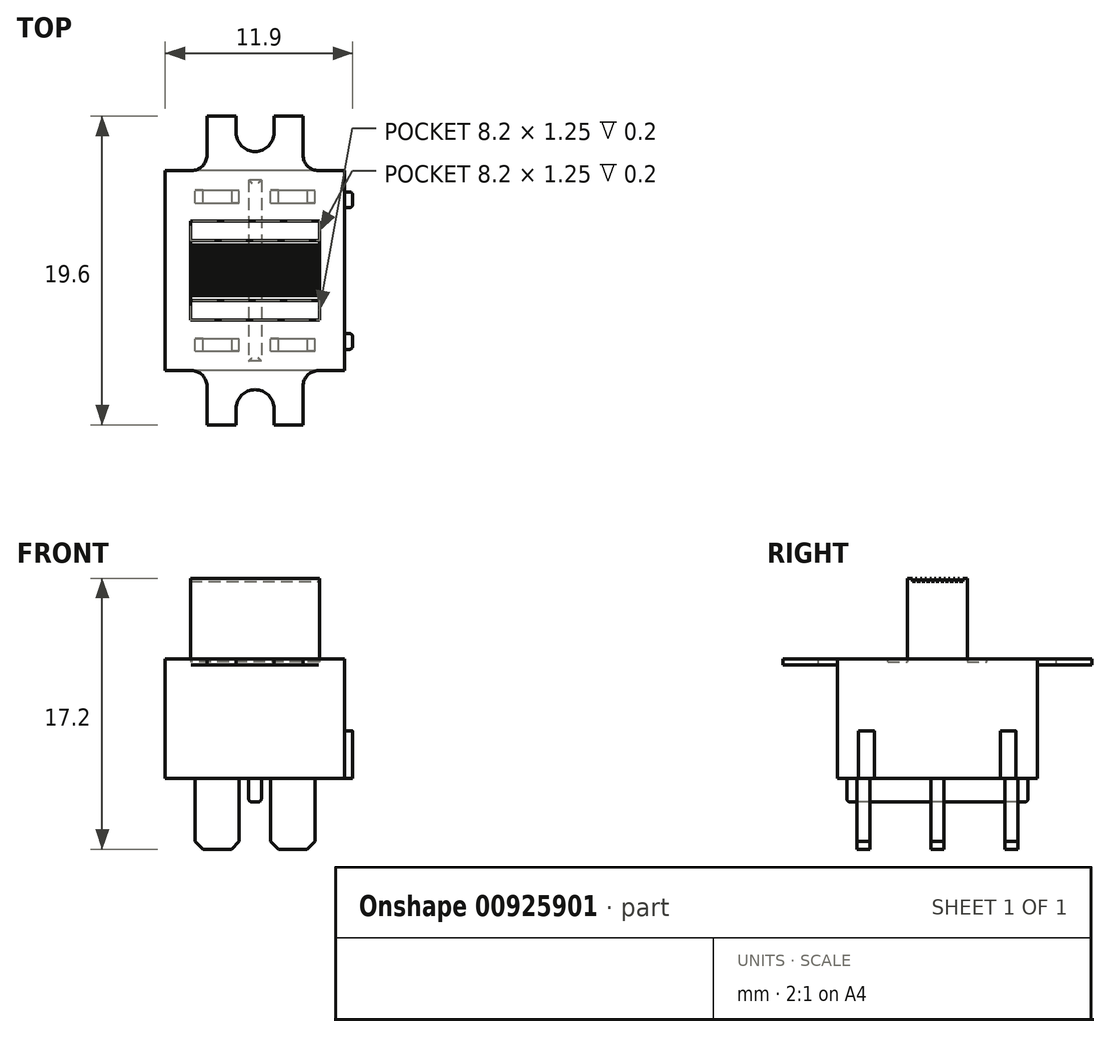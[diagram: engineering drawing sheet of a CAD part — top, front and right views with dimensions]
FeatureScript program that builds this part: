
annotation { "Feature Type Name" : "Feature", "Feature Type Description" : "" }
export const myFeature = defineFeature(function(context is Context, id is Id, definition is map)
    precondition{}
    {
        {
            var Q0;
            Q0=qCreatedBy(makeId("Top.planeOp"),FACE);
            var sketch = newSketch(context, id + "F0", { "sketchPlane" : qUnion([Q0])});
            skLineSegment(sketch, "E0.bottom", {"start": v(5.7, -6.35) * mm, "end": v(-5.7, -6.35) * mm});
            skLineSegment(sketch, "E0.top", {"start": v(5.7, 6.35) * mm, "end": v(-5.7, 6.35) * mm});
            skLineSegment(sketch, "E0.left", {"start": v(5.7, -6.35) * mm, "end": v(5.7, 6.35) * mm});
            skLineSegment(sketch, "E0.right", {"start": v(-5.7, -6.35) * mm, "end": v(-5.7, 6.35) * mm});
            skPoint(sketch, "E0.middle", {"position": v(0, 0) * mm});
            skLineSegment(sketch, "E1.bottom", {"start": v(3.05, -9.8) * mm, "end": v(-3.05, -9.8) * mm});
            skLineSegment(sketch, "E1.top", {"start": v(3.05, 9.8) * mm, "end": v(-3.05, 9.8) * mm});
            skLineSegment(sketch, "E1.left", {"start": v(3.05, -9.8) * mm, "end": v(3.05, 9.8) * mm});
            skLineSegment(sketch, "E1.right", {"start": v(-3.05, -9.8) * mm, "end": v(-3.05, 9.8) * mm});
            skSolve(sketch);
        }
        {
            var Q0;
            Q0 = qSketchRegion(id + "F0", true);
            extrude(context, id + "F1", {"entities" : qUnion([Q0]), "depth" : 0.4 * mm, "offsetDistance" : 25 * mm});
        }
        {
            var Q0;
            Q0=makeQuery(id+"F1.opExtrude","CAP_FACE",FACE,{"disambiguationData":[OSD([sQuery(id+"F0.wireOp",EDGE,"E0.bottom"),sQuery(id+"F0.wireOp",EDGE,"E0.top"),sQuery(id+"F0.wireOp",EDGE,"E0.left"),sQuery(id+"F0.wireOp",EDGE,"E0.right"),sQuery(id+"F0.wireOp",EDGE,"E1.bottom"),sQuery(id+"F0.wireOp",EDGE,"E1.top"),sQuery(id+"F0.wireOp",EDGE,"E1.left"),sQuery(id+"F0.wireOp",EDGE,"E1.right")])],"isStart":false});
            var sketch = newSketch(context, id + "F2", { "sketchPlane" : qUnion([Q0])});
            skLineSegment(sketch, "E2", {"start": v(-4.12, 8.77) * mm, "end": v(4.46, 8.77) * mm, "construction": true});
            skLineSegment(sketch, "E3", {"start": v(-3.99, -8.77) * mm, "end": v(4.43, -8.77) * mm, "construction": true});
            skArc(sketch, "E4", {"start": v(1.2, 8.77) * mm, "mid": v(0, 7.57) * mm, "end": v(-1.2, 8.77) * mm});
            skArc(sketch, "E5", {"start": v(1.2, -8.77) * mm, "mid": v(0, -7.57) * mm, "end": v(-1.2, -8.77) * mm});
            skLineSegment(sketch, "E6.bottom", {"start": v(-1.2, 8.77) * mm, "end": v(1.2, 8.77) * mm});
            skLineSegment(sketch, "E6.top", {"start": v(-1.2, 9.8) * mm, "end": v(1.2, 9.8) * mm});
            skLineSegment(sketch, "E6.left", {"start": v(-1.2, 8.77) * mm, "end": v(-1.2, 9.8) * mm});
            skLineSegment(sketch, "E6.right", {"start": v(1.2, 8.77) * mm, "end": v(1.2, 9.8) * mm});
            skLineSegment(sketch, "E7.bottom", {"start": v(-1.2, -8.77) * mm, "end": v(1.2, -8.77) * mm});
            skLineSegment(sketch, "E7.top", {"start": v(-1.2, -9.8) * mm, "end": v(1.2, -9.8) * mm});
            skLineSegment(sketch, "E7.left", {"start": v(-1.2, -8.77) * mm, "end": v(-1.2, -9.8) * mm});
            skLineSegment(sketch, "E7.right", {"start": v(1.2, -8.77) * mm, "end": v(1.2, -9.8) * mm});
            skSolve(sketch);
        }
        {
            var Q0;
            Q0 = qSketchRegion(id + "F2", true);
            extrude(context, id + "F3", {"entities" : qUnion([Q0]), "operationType" : NewBodyOperationType.REMOVE, "oppositeDirection" : true, "depth" : 1 * mm, "offsetDistance" : 25 * mm});
        }
        {
            var Q0;
            Q0=makeQuery(id+"F1.opExtrude","CAP_FACE",FACE,{"disambiguationData":[OSD([sQuery(id+"F0.wireOp",EDGE,"E0.bottom"),sQuery(id+"F0.wireOp",EDGE,"E0.top"),sQuery(id+"F0.wireOp",EDGE,"E0.left"),sQuery(id+"F0.wireOp",EDGE,"E0.right"),sQuery(id+"F0.wireOp",EDGE,"E1.bottom"),sQuery(id+"F0.wireOp",EDGE,"E1.top"),sQuery(id+"F0.wireOp",EDGE,"E1.left"),sQuery(id+"F0.wireOp",EDGE,"E1.right")])],"isStart":false});
            var sketch = newSketch(context, id + "F4", { "sketchPlane" : qUnion([Q0])});
            skLineSegment(sketch, "E8.bottom", {"start": v(4.1, -3.15) * mm, "end": v(-4.1, -3.15) * mm});
            skLineSegment(sketch, "E8.top", {"start": v(4.1, 3.15) * mm, "end": v(-4.1, 3.15) * mm});
            skLineSegment(sketch, "E8.left", {"start": v(4.1, -3.15) * mm, "end": v(4.1, 3.15) * mm});
            skLineSegment(sketch, "E8.right", {"start": v(-4.1, -3.15) * mm, "end": v(-4.1, 3.15) * mm});
            skPoint(sketch, "E8.middle", {"position": v(0, 0) * mm});
            skSolve(sketch);
        }
        {
            var Q0;
            Q0 = qSketchRegion(id + "F4", true);
            extrude(context, id + "F5", {"entities" : qUnion([Q0]), "operationType" : NewBodyOperationType.REMOVE, "oppositeDirection" : true, "depth" : 0.2 * mm, "offsetDistance" : 25 * mm});
        }
        {
            var Q0;
            Q0=makeQuery(id+"F5.boolean.opBoolean","COPY",FACE,{"derivedFrom":makeQuery(id+"F5.opExtrude","CAP_FACE",FACE,{"disambiguationData":[OSD([sQuery(id+"F4.wireOp",EDGE,"E8.bottom"),sQuery(id+"F4.wireOp",EDGE,"E8.top"),sQuery(id+"F4.wireOp",EDGE,"E8.left"),sQuery(id+"F4.wireOp",EDGE,"E8.right")])],"isStart":false})});
            var sketch = newSketch(context, id + "F6", { "sketchPlane" : qUnion([Q0])});
            skLineSegment(sketch, "E9.bottom", {"start": v(4.1, -1.9) * mm, "end": v(-4.1, -1.9) * mm});
            skLineSegment(sketch, "E9.top", {"start": v(4.1, 1.9) * mm, "end": v(-4.1, 1.9) * mm});
            skLineSegment(sketch, "E9.left", {"start": v(4.1, -1.9) * mm, "end": v(4.1, 1.9) * mm});
            skLineSegment(sketch, "E9.right", {"start": v(-4.1, -1.9) * mm, "end": v(-4.1, 1.9) * mm});
            skPoint(sketch, "E9.middle", {"position": v(0, 0) * mm});
            skSolve(sketch);
        }
        {
            var Q0;
            Q0 = qSketchRegion(id + "F6", true);
            extrude(context, id + "F7", {"entities" : qUnion([Q0]), "operationType" : NewBodyOperationType.ADD, "depth" : 5.3 * mm, "offsetDistance" : 25 * mm});
        }
        {
            var Q0;
            Q0=makeQuery(id+"F1.opExtrude","CAP_FACE",FACE,{"disambiguationData":[OSD([sQuery(id+"F0.wireOp",EDGE,"E0.bottom"),sQuery(id+"F0.wireOp",EDGE,"E0.top"),sQuery(id+"F0.wireOp",EDGE,"E0.left"),sQuery(id+"F0.wireOp",EDGE,"E0.right"),sQuery(id+"F0.wireOp",EDGE,"E1.bottom"),sQuery(id+"F0.wireOp",EDGE,"E1.top"),sQuery(id+"F0.wireOp",EDGE,"E1.left"),sQuery(id+"F0.wireOp",EDGE,"E1.right")])],"isStart":true});
            var sketch = newSketch(context, id + "F8", { "sketchPlane" : qUnion([Q0])});
            skLineSegment(sketch, "E10.bottom", {"start": v(5.7, -6.35) * mm, "end": v(-5.7, -6.35) * mm});
            skLineSegment(sketch, "E10.top", {"start": v(5.7, 6.35) * mm, "end": v(-5.7, 6.35) * mm});
            skLineSegment(sketch, "E10.left", {"start": v(5.7, -6.35) * mm, "end": v(5.7, 6.35) * mm});
            skLineSegment(sketch, "E10.right", {"start": v(-5.7, -6.35) * mm, "end": v(-5.7, 6.35) * mm});
            skPoint(sketch, "E10.middle", {"position": v(0, 0) * mm});
            skSolve(sketch);
        }
        {
            var Q0;
            Q0 = qSketchRegion(id + "F8", true);
            extrude(context, id + "F9", {"entities" : qUnion([Q0]), "operationType" : NewBodyOperationType.ADD, "depth" : 7.2 * mm, "offsetDistance" : 25 * mm});
        }
        {
            var Q0;
            Q0=makeQuery(id+"F9.boolean.opBoolean","MERGE",FACE,{"derivedFrom":[makeQuery(id+"F1.opExtrude","SWEPT_FACE",FACE,{"disambiguationData":[OSD([sQuery(id+"F0.wireOp",EDGE,"E0.left")])]}),makeQuery(id+"F9.opExtrude","SWEPT_FACE",FACE,{"disambiguationData":[OSD([sQuery(id+"F8.wireOp",EDGE,"E10.left")])]})]});
            var sketch = newSketch(context, id + "F10", { "sketchPlane" : qUnion([Q0])});
            skLineSegment(sketch, "E11.bottom", {"start": v(5, -7.2) * mm, "end": v(4, -7.2) * mm});
            skLineSegment(sketch, "E11.top", {"start": v(5, -4.2) * mm, "end": v(4, -4.2) * mm});
            skLineSegment(sketch, "E11.left", {"start": v(5, -7.2) * mm, "end": v(5, -4.2) * mm});
            skLineSegment(sketch, "E11.right", {"start": v(4, -7.2) * mm, "end": v(4, -4.2) * mm});
            skLineSegment(sketch, "E12.bottom", {"start": v(-4, -7.2) * mm, "end": v(-5, -7.2) * mm});
            skLineSegment(sketch, "E12.top", {"start": v(-4, -4.2) * mm, "end": v(-5, -4.2) * mm});
            skLineSegment(sketch, "E12.left", {"start": v(-4, -7.2) * mm, "end": v(-4, -4.2) * mm});
            skLineSegment(sketch, "E12.right", {"start": v(-5, -7.2) * mm, "end": v(-5, -4.2) * mm});
            skSolve(sketch);
        }
        {
            var Q0;
            Q0 = qSketchRegion(id + "F10", true);
            extrude(context, id + "F11", {"entities" : qUnion([Q0]), "operationType" : NewBodyOperationType.ADD, "depth" : 0.5 * mm, "offsetDistance" : 25 * mm});
        }
        {
            var Q0;
            Q0=makeQuery(id+"F11.boolean.opBoolean","MERGE",FACE,{"derivedFrom":[makeQuery(id+"F9.opExtrude","CAP_FACE",FACE,{"disambiguationData":[OSD([sQuery(id+"F8.wireOp",EDGE,"E10.bottom"),sQuery(id+"F8.wireOp",EDGE,"E10.top"),sQuery(id+"F8.wireOp",EDGE,"E10.left"),sQuery(id+"F8.wireOp",EDGE,"E10.right")])],"isStart":false}),makeQuery(id+"F11.opExtrude","SWEPT_FACE",FACE,{"disambiguationData":[OSD([sQuery(id+"F10.wireOp",EDGE,"E11.bottom")])]}),makeQuery(id+"F11.opExtrude","SWEPT_FACE",FACE,{"disambiguationData":[OSD([sQuery(id+"F10.wireOp",EDGE,"E12.bottom")])]})]});
            var sketch = newSketch(context, id + "F12", { "sketchPlane" : qUnion([Q0])});
            skLineSegment(sketch, "E13.bottom", {"start": v(1, -4.3) * mm, "end": v(3.8, -4.3) * mm});
            skLineSegment(sketch, "E13.top", {"start": v(1, -5.1) * mm, "end": v(3.8, -5.1) * mm});
            skLineSegment(sketch, "E13.left", {"start": v(1, -4.3) * mm, "end": v(1, -5.1) * mm});
            skLineSegment(sketch, "E13.right", {"start": v(3.8, -4.3) * mm, "end": v(3.8, -5.1) * mm});
            skPoint(sketch, "E13.middle", {"position": v(2.4, -4.7) * mm});
            skLineSegment(sketch, "E14.0.1.0", {"start": v(1, -0.4) * mm, "end": v(3.8, -0.4) * mm});
            skLineSegment(sketch, "E14.0.1.1", {"start": v(1, 0.4) * mm, "end": v(1, -0.4) * mm});
            skLineSegment(sketch, "E14.0.1.2", {"start": v(1, 0.4) * mm, "end": v(3.8, 0.4) * mm});
            skLineSegment(sketch, "E14.0.1.3", {"start": v(3.8, 0.4) * mm, "end": v(3.8, -0.4) * mm});
            skLineSegment(sketch, "E14.0.2.0", {"start": v(1, 4.3) * mm, "end": v(3.8, 4.3) * mm});
            skLineSegment(sketch, "E14.0.2.1", {"start": v(1, 5.1) * mm, "end": v(1, 4.3) * mm});
            skLineSegment(sketch, "E14.0.2.2", {"start": v(1, 5.1) * mm, "end": v(3.8, 5.1) * mm});
            skLineSegment(sketch, "E14.0.2.3", {"start": v(3.8, 5.1) * mm, "end": v(3.8, 4.3) * mm});
            skLineSegment(sketch, "E14.1.0.0", {"start": v(-3.8, -5.1) * mm, "end": v(-1, -5.1) * mm});
            skLineSegment(sketch, "E14.1.0.1", {"start": v(-3.8, -4.3) * mm, "end": v(-3.8, -5.1) * mm});
            skLineSegment(sketch, "E14.1.0.2", {"start": v(-3.8, -4.3) * mm, "end": v(-1, -4.3) * mm});
            skLineSegment(sketch, "E14.1.0.3", {"start": v(-1, -4.3) * mm, "end": v(-1, -5.1) * mm});
            skLineSegment(sketch, "E14.1.1.0", {"start": v(-3.8, -0.4) * mm, "end": v(-1, -0.4) * mm});
            skLineSegment(sketch, "E14.1.1.1", {"start": v(-3.8, 0.4) * mm, "end": v(-3.8, -0.4) * mm});
            skLineSegment(sketch, "E14.1.1.2", {"start": v(-3.8, 0.4) * mm, "end": v(-1, 0.4) * mm});
            skLineSegment(sketch, "E14.1.1.3", {"start": v(-1, 0.4) * mm, "end": v(-1, -0.4) * mm});
            skLineSegment(sketch, "E14.1.2.0", {"start": v(-3.8, 4.3) * mm, "end": v(-1, 4.3) * mm});
            skLineSegment(sketch, "E14.1.2.1", {"start": v(-3.8, 5.1) * mm, "end": v(-3.8, 4.3) * mm});
            skLineSegment(sketch, "E14.1.2.2", {"start": v(-3.8, 5.1) * mm, "end": v(-1, 5.1) * mm});
            skLineSegment(sketch, "E14.1.2.3", {"start": v(-1, 5.1) * mm, "end": v(-1, 4.3) * mm});
            skLineSegment(sketch, "E14.direction1", {"start": v(1, -5.1) * mm, "end": v(-3.8, -5.1) * mm, "construction": true});
            skLineSegment(sketch, "E14.direction2", {"start": v(1, -5.1) * mm, "end": v(1, -0.4) * mm, "construction": true});
            skSolve(sketch);
        }
        {
            var Q0;
            Q0 = qSketchRegion(id + "F12", true);
            extrude(context, id + "F13", {"entities" : qUnion([Q0]), "operationType" : NewBodyOperationType.ADD, "depth" : 4.5 * mm, "offsetDistance" : 25 * mm});
        }
        {
            var Q0;
            Q0=makeQuery(id+"F1.opExtrude","SWEPT_EDGE",EDGE,{"disambiguationData":[OSD([sQuery(id+"F0.wireOp",EDGE,"E0.top"),sQuery(id+"F0.wireOp",EDGE,"E1.left")])]});
            var Q1;
            Q1=makeQuery(id+"F1.opExtrude","SWEPT_EDGE",EDGE,{"disambiguationData":[OSD([sQuery(id+"F0.wireOp",EDGE,"E0.top"),sQuery(id+"F0.wireOp",EDGE,"E1.right")])]});
            var Q2;
            Q2=makeQuery(id+"F1.opExtrude","SWEPT_EDGE",EDGE,{"disambiguationData":[OSD([sQuery(id+"F0.wireOp",EDGE,"E0.bottom"),sQuery(id+"F0.wireOp",EDGE,"E1.left")])]});
            var Q3;
            Q3=makeQuery(id+"F1.opExtrude","SWEPT_EDGE",EDGE,{"disambiguationData":[OSD([sQuery(id+"F0.wireOp",EDGE,"E0.bottom"),sQuery(id+"F0.wireOp",EDGE,"E1.right")])]});
            fillet(context, id + "F14", {"entities" : qUnion([Q0, Q1, Q2, Q3]), "radius" : 1 * mm, "tangentPropagation" : true, "allowEdgeOverflow" : false});
        }
        {
            var Q0;
            Q0=makeQuery(id+"F13.opExtrude","CAP_EDGE",EDGE,{"disambiguationData":[OSD([sQuery(id+"F12.wireOp",EDGE,"E13.left")])],"isStart":false});
            var Q1;
            Q1=makeQuery(id+"F13.opExtrude","CAP_EDGE",EDGE,{"disambiguationData":[OSD([sQuery(id+"F12.wireOp",EDGE,"E13.right")])],"isStart":false});
            var Q2;
            Q2=makeQuery(id+"F13.opExtrude","CAP_EDGE",EDGE,{"disambiguationData":[OSD([sQuery(id+"F12.wireOp",EDGE,"E14.1.0.3")])],"isStart":false});
            var Q3;
            Q3=makeQuery(id+"F13.opExtrude","CAP_EDGE",EDGE,{"disambiguationData":[OSD([sQuery(id+"F12.wireOp",EDGE,"E14.1.0.1")])],"isStart":false});
            var Q4;
            Q4=makeQuery(id+"F13.opExtrude","CAP_EDGE",EDGE,{"disambiguationData":[OSD([sQuery(id+"F12.wireOp",EDGE,"E14.0.1.1")])],"isStart":false});
            var Q5;
            Q5=makeQuery(id+"F13.opExtrude","CAP_EDGE",EDGE,{"disambiguationData":[OSD([sQuery(id+"F12.wireOp",EDGE,"E14.0.1.3")])],"isStart":false});
            var Q6;
            Q6=makeQuery(id+"F13.opExtrude","CAP_EDGE",EDGE,{"disambiguationData":[OSD([sQuery(id+"F12.wireOp",EDGE,"E14.1.1.3")])],"isStart":false});
            var Q7;
            Q7=makeQuery(id+"F13.opExtrude","CAP_EDGE",EDGE,{"disambiguationData":[OSD([sQuery(id+"F12.wireOp",EDGE,"E14.1.1.1")])],"isStart":false});
            var Q8;
            Q8=makeQuery(id+"F13.opExtrude","CAP_EDGE",EDGE,{"disambiguationData":[OSD([sQuery(id+"F12.wireOp",EDGE,"E14.1.2.1")])],"isStart":false});
            var Q9;
            Q9=makeQuery(id+"F13.opExtrude","CAP_EDGE",EDGE,{"disambiguationData":[OSD([sQuery(id+"F12.wireOp",EDGE,"E14.1.2.3")])],"isStart":false});
            var Q10;
            Q10=makeQuery(id+"F13.opExtrude","CAP_EDGE",EDGE,{"disambiguationData":[OSD([sQuery(id+"F12.wireOp",EDGE,"E14.0.2.1")])],"isStart":false});
            var Q11;
            Q11=makeQuery(id+"F13.opExtrude","CAP_EDGE",EDGE,{"disambiguationData":[OSD([sQuery(id+"F12.wireOp",EDGE,"E14.0.2.3")])],"isStart":false});
            chamfer(context, id + "F15", {"entities" : qUnion([Q0, Q1, Q2, Q3, Q4, Q5, Q6, Q7, Q8, Q9, Q10, Q11]), "width" : 0.5 * mm, "tangentPropagation" : true});
        }
        {
            var Q0;
            Q0=makeQuery(id+"F11.boolean.opBoolean","MERGE",FACE,{"derivedFrom":[makeQuery(id+"F9.opExtrude","CAP_FACE",FACE,{"disambiguationData":[OSD([sQuery(id+"F8.wireOp",EDGE,"E10.bottom"),sQuery(id+"F8.wireOp",EDGE,"E10.top"),sQuery(id+"F8.wireOp",EDGE,"E10.left"),sQuery(id+"F8.wireOp",EDGE,"E10.right")])],"isStart":false}),makeQuery(id+"F11.opExtrude","SWEPT_FACE",FACE,{"disambiguationData":[OSD([sQuery(id+"F10.wireOp",EDGE,"E11.bottom")])]}),makeQuery(id+"F11.opExtrude","SWEPT_FACE",FACE,{"disambiguationData":[OSD([sQuery(id+"F10.wireOp",EDGE,"E12.bottom")])]})]});
            var sketch = newSketch(context, id + "F16", { "sketchPlane" : qUnion([Q0])});
            skLineSegment(sketch, "E15.bottom", {"start": v(0.4, -5.75) * mm, "end": v(-0.4, -5.75) * mm});
            skLineSegment(sketch, "E15.top", {"start": v(0.4, 5.75) * mm, "end": v(-0.4, 5.75) * mm});
            skLineSegment(sketch, "E15.left", {"start": v(0.4, -5.75) * mm, "end": v(0.4, 5.75) * mm});
            skLineSegment(sketch, "E15.right", {"start": v(-0.4, -5.75) * mm, "end": v(-0.4, 5.75) * mm});
            skPoint(sketch, "E15.middle", {"position": v(0, 0) * mm});
            skSolve(sketch);
        }
        {
            var Q0;
            Q0 = qSketchRegion(id + "F16", true);
            extrude(context, id + "F17", {"entities" : qUnion([Q0]), "operationType" : NewBodyOperationType.ADD, "depth" : 1.5 * mm, "offsetDistance" : 25 * mm});
        }
        {
            var Q0;
            Q0=makeQuery(id+"F17.opExtrude","CAP_EDGE",EDGE,{"disambiguationData":[OSD([sQuery(id+"F16.wireOp",EDGE,"E15.top")])],"isStart":false});
            var Q1;
            Q1=makeQuery(id+"F17.opExtrude","CAP_EDGE",EDGE,{"disambiguationData":[OSD([sQuery(id+"F16.wireOp",EDGE,"E15.bottom")])],"isStart":false});
            var Q2;
            Q2=makeQuery(id+"F17.opExtrude","CAP_EDGE",EDGE,{"disambiguationData":[OSD([sQuery(id+"F16.wireOp",EDGE,"E15.left")])],"isStart":false});
            var Q3;
            Q3=makeQuery(id+"F17.opExtrude","CAP_EDGE",EDGE,{"disambiguationData":[OSD([sQuery(id+"F16.wireOp",EDGE,"E15.right")])],"isStart":false});
            var Q4;
            Q4=makeQuery(id+"F11.opExtrude","CAP_EDGE",EDGE,{"disambiguationData":[OSD([sQuery(id+"F10.wireOp",EDGE,"E12.right")])],"isStart":false});
            var Q5;
            Q5=makeQuery(id+"F11.opExtrude","CAP_EDGE",EDGE,{"disambiguationData":[OSD([sQuery(id+"F10.wireOp",EDGE,"E12.left")])],"isStart":false});
            var Q6;
            Q6=makeQuery(id+"F11.opExtrude","CAP_EDGE",EDGE,{"disambiguationData":[OSD([sQuery(id+"F10.wireOp",EDGE,"E11.left")])],"isStart":false});
            var Q7;
            Q7=makeQuery(id+"F11.opExtrude","CAP_EDGE",EDGE,{"disambiguationData":[OSD([sQuery(id+"F10.wireOp",EDGE,"E11.right")])],"isStart":false});
            fillet(context, id + "F18", {"entities" : qUnion([Q0, Q1, Q2, Q3, Q4, Q5, Q6, Q7]), "radius" : 0.2 * mm, "tangentPropagation" : true, "allowEdgeOverflow" : false});
        }
        {
            var Q0;
            Q0=makeQuery(id+"F7.opExtrude","SWEPT_FACE",FACE,{"disambiguationData":[OSD([sQuery(id+"F6.wireOp",EDGE,"E9.left")])]});
            var sketch = newSketch(context, id + "F19", { "sketchPlane" : qUnion([Q0])});
            skLineSegment(sketch, "E16.bottom", {"start": v(-1.6, 5.5) * mm, "end": v(-1.4, 5.5) * mm});
            skLineSegment(sketch, "E16.top", {"start": v(-1.6, 5.3) * mm, "end": v(-1.4, 5.3) * mm});
            skLineSegment(sketch, "E16.left", {"start": v(-1.6, 5.5) * mm, "end": v(-1.6, 5.3) * mm});
            skLineSegment(sketch, "E16.right", {"start": v(-1.4, 5.5) * mm, "end": v(-1.4, 5.3) * mm});
            skLineSegment(sketch, "E17.1.0.0", {"start": v(-1.1, 5.5) * mm, "end": v(-1.1, 5.3) * mm});
            skLineSegment(sketch, "E17.1.0.1", {"start": v(-1.3, 5.5) * mm, "end": v(-1.1, 5.5) * mm});
            skLineSegment(sketch, "E17.1.0.2", {"start": v(-1.3, 5.5) * mm, "end": v(-1.3, 5.3) * mm});
            skLineSegment(sketch, "E17.1.0.3", {"start": v(-1.3, 5.3) * mm, "end": v(-1.1, 5.3) * mm});
            skLineSegment(sketch, "E17.2.0.0", {"start": v(-0.8, 5.5) * mm, "end": v(-0.8, 5.3) * mm});
            skLineSegment(sketch, "E17.2.0.1", {"start": v(-1, 5.5) * mm, "end": v(-0.8, 5.5) * mm});
            skLineSegment(sketch, "E17.2.0.2", {"start": v(-1, 5.5) * mm, "end": v(-1, 5.3) * mm});
            skLineSegment(sketch, "E17.2.0.3", {"start": v(-1, 5.3) * mm, "end": v(-0.8, 5.3) * mm});
            skLineSegment(sketch, "E17.3.0.0", {"start": v(-0.5, 5.5) * mm, "end": v(-0.5, 5.3) * mm});
            skLineSegment(sketch, "E17.3.0.1", {"start": v(-0.7, 5.5) * mm, "end": v(-0.5, 5.5) * mm});
            skLineSegment(sketch, "E17.3.0.2", {"start": v(-0.7, 5.5) * mm, "end": v(-0.7, 5.3) * mm});
            skLineSegment(sketch, "E17.3.0.3", {"start": v(-0.7, 5.3) * mm, "end": v(-0.5, 5.3) * mm});
            skLineSegment(sketch, "E17.4.0.0", {"start": v(-0.2, 5.5) * mm, "end": v(-0.2, 5.3) * mm});
            skLineSegment(sketch, "E17.4.0.1", {"start": v(-0.4, 5.5) * mm, "end": v(-0.2, 5.5) * mm});
            skLineSegment(sketch, "E17.4.0.2", {"start": v(-0.4, 5.5) * mm, "end": v(-0.4, 5.3) * mm});
            skLineSegment(sketch, "E17.4.0.3", {"start": v(-0.4, 5.3) * mm, "end": v(-0.2, 5.3) * mm});
            skLineSegment(sketch, "E17.5.0.0", {"start": v(0.1, 5.5) * mm, "end": v(0.1, 5.3) * mm});
            skLineSegment(sketch, "E17.5.0.1", {"start": v(-0.1, 5.5) * mm, "end": v(0.1, 5.5) * mm});
            skLineSegment(sketch, "E17.5.0.2", {"start": v(-0.1, 5.5) * mm, "end": v(-0.1, 5.3) * mm});
            skLineSegment(sketch, "E17.5.0.3", {"start": v(-0.1, 5.3) * mm, "end": v(0.1, 5.3) * mm});
            skLineSegment(sketch, "E17.6.0.0", {"start": v(0.4, 5.5) * mm, "end": v(0.4, 5.3) * mm});
            skLineSegment(sketch, "E17.6.0.1", {"start": v(0.2, 5.5) * mm, "end": v(0.4, 5.5) * mm});
            skLineSegment(sketch, "E17.6.0.2", {"start": v(0.2, 5.5) * mm, "end": v(0.2, 5.3) * mm});
            skLineSegment(sketch, "E17.6.0.3", {"start": v(0.2, 5.3) * mm, "end": v(0.4, 5.3) * mm});
            skLineSegment(sketch, "E17.7.0.0", {"start": v(0.7, 5.5) * mm, "end": v(0.7, 5.3) * mm});
            skLineSegment(sketch, "E17.7.0.1", {"start": v(0.5, 5.5) * mm, "end": v(0.7, 5.5) * mm});
            skLineSegment(sketch, "E17.7.0.2", {"start": v(0.5, 5.5) * mm, "end": v(0.5, 5.3) * mm});
            skLineSegment(sketch, "E17.7.0.3", {"start": v(0.5, 5.3) * mm, "end": v(0.7, 5.3) * mm});
            skLineSegment(sketch, "E17.8.0.0", {"start": v(1, 5.5) * mm, "end": v(1, 5.3) * mm});
            skLineSegment(sketch, "E17.8.0.1", {"start": v(0.8, 5.5) * mm, "end": v(1, 5.5) * mm});
            skLineSegment(sketch, "E17.8.0.2", {"start": v(0.8, 5.5) * mm, "end": v(0.8, 5.3) * mm});
            skLineSegment(sketch, "E17.8.0.3", {"start": v(0.8, 5.3) * mm, "end": v(1, 5.3) * mm});
            skLineSegment(sketch, "E17.9.0.0", {"start": v(1.3, 5.5) * mm, "end": v(1.3, 5.3) * mm});
            skLineSegment(sketch, "E17.9.0.1", {"start": v(1.1, 5.5) * mm, "end": v(1.3, 5.5) * mm});
            skLineSegment(sketch, "E17.9.0.2", {"start": v(1.1, 5.5) * mm, "end": v(1.1, 5.3) * mm});
            skLineSegment(sketch, "E17.9.0.3", {"start": v(1.1, 5.3) * mm, "end": v(1.3, 5.3) * mm});
            skLineSegment(sketch, "E17.10.0.0", {"start": v(1.6, 5.5) * mm, "end": v(1.6, 5.3) * mm});
            skLineSegment(sketch, "E17.10.0.1", {"start": v(1.4, 5.5) * mm, "end": v(1.6, 5.5) * mm});
            skLineSegment(sketch, "E17.10.0.2", {"start": v(1.4, 5.5) * mm, "end": v(1.4, 5.3) * mm});
            skLineSegment(sketch, "E17.10.0.3", {"start": v(1.4, 5.3) * mm, "end": v(1.6, 5.3) * mm});
            skLineSegment(sketch, "E17.direction1", {"start": v(-1.4, 5.3) * mm, "end": v(-1.1, 5.3) * mm, "construction": true});
            skSolve(sketch);
        }
        {
            var Q0;
            Q0 = qSketchRegion(id + "F19", true);
            extrude(context, id + "F20", {"entities" : qUnion([Q0]), "operationType" : NewBodyOperationType.REMOVE, "oppositeDirection" : true, "depth" : 25 * mm, "offsetDistance" : 25 * mm});
        }
    });
